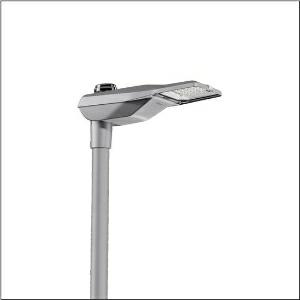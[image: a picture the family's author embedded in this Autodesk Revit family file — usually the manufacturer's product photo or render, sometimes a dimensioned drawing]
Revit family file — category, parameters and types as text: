
# Revit family: streetlight_sl_21_micro___p0_8a_5xe5u27n08cb_fa48
name_source: partatom
category: Lighting Fixtures
units: mm (PartAtom-declared; Revit-internal decimal feet)

## family parameters
Cut with Voids When Loaded = No
Host = Face
Light Source = No
Part Type = Normal
Room Calculation Point = No
Round Connector Dimension = Use Diameter
Shared = No

## types (1)
- --- (1 x LED, 1870 lm, 15.8 W, 2200K)
    Apparent Load = 16 VA
    CIE Flux Codes = 33 69 96 100 100
    Color Rendering = 70
    Color Temperature = 2200K
    Default Elevation = 1800 mm
    Description = Streetlight SL 21 micro, mast luminaire, primary light control with lens, of PMMA, primary optical cover: cover, of toughened safety glass, transparent, light distribution: P0.8a, light emission: direct distribution, primary light characteristic: asymmetric, installation type: post-top, LED, 3G 1.5mm², High Power LED, rated luminous flux: 1.870lm, luminous efficacy: 118lm/W, light colour: 722, colour temperature: 2200K, control gear: NEMA (7pin), control: flexible luminous flux parameterisation, time-dependent luminous flux control, constant luminous flux control, pre-setting: linear dimming characteristic, overheat protection, mains connection: 230..240V, AC, 50/60Hz, connection cable pre-assembled, cable length: 6,5m, wiring characteristics: H07RN-F, start of lifetime: 16W, end of service life: 16W, reduction: 8W, luminaire housing, of diecast aluminium (EN AC-44300), powder-coated, SITECO metallic grey (DB 702S), corrosivity category C5 high according to DIN EN ISO 12944, multi-level sealing system, sealing non-destructively replaceable, inclination adjustable: 0°, 5°, 10°, 15°, length: 528mm, width: 235mm, height: 110mm, spigot size: 76/60mm (post-top), mounting height: 4..8m, protection rating (complete): IP66, insulation class (complete): insulation class I (protective earthing), certification: CE, ENEC, ENEC+, VDE, impact resistance: IK10, permissible operating ambient temperature for outdoor applications: -40..+50°C, standard-compliant lighting for roads and squares, packaging unit: 1 piece

Light Distribution: P0.8a
    Height = 110 mm
    Lamp = 1 x LED
    Lamp Light Flux = 1870 lm
    Lamp Power = 15.8 W
    Lamp count = 1
    Length = 528 mm
    Luminous efficacy = 118 lm/W
    Manufacturer = Siteco
    ModVariant = No
    Model = 5XE5U27N08CB
    Number of Poles = 1
    OnlyDefault = Yes
    Power Factor = 1
    Product Name = Streetlight SL 21 micro | P0.8a
    Product group = mast luminaire | pylon top
    ProductGroupID = 6100
    Protection Class = Protection class I
    Protection Degree = IP 66
    RLX_Detail_Level = 1
    RLX_Emergency_Light_Flux = 0 lm
    RLX_Emergency_Type = 0
    RLX_Emergency_Type_DB = No
    RlxData = <blob elided: 98377 chars, md5=81ff22f5>
    Socket = socket
    Standby Power = 0 W
    System Light Flux = 1870 lm
    System Power = 16 W
    Type Comments = factory setting: luminous flux: 100 % | dim-lin: 254 | 300 mA
    Type Image = l_1294375.jpg
    URL = http://relux.com
    VarID = @adj_081617
    Voltage = 0 V
    Weight = 0.00 kg
    Width = 235 mm

## geometry (parser evidence)
native form markers: Blend x4, Sweep x9
no freeform markers — native parametric forms only
